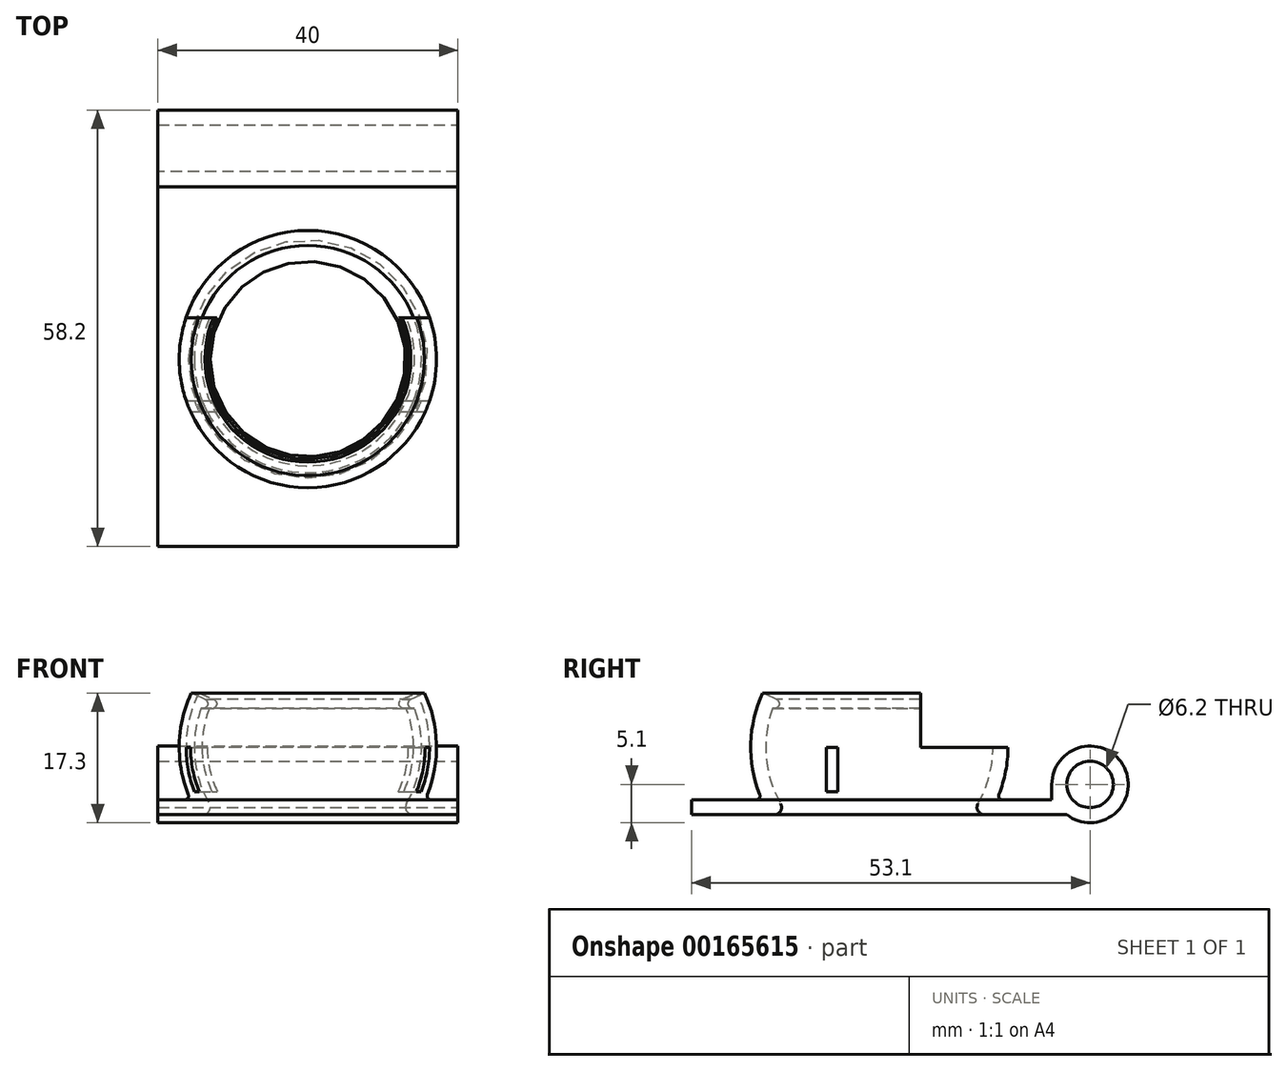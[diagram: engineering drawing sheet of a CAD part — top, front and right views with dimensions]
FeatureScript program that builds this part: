
annotation { "Feature Type Name" : "Feature", "Feature Type Description" : "" }
export const myFeature = defineFeature(function(context is Context, id is Id, definition is map)
    precondition{}
    {
        {
            var Q0;
            Q0=qCreatedBy(makeId("Front.planeOp"),FACE);
            var sketch = newSketch(context, id + "F0", { "sketchPlane" : qUnion([Q0])});
            skArc(sketch, "E0", {"start": v(-4.55, 14.3) * mm, "mid": v(-14.58, 3.55) * mm, "end": v(-10.6, -10.6) * mm});
            skLineSegment(sketch, "E1", {"start": v(-4.55, 14.3) * mm, "end": v(-4.55, 0) * mm});
            skLineSegment(sketch, "E2", {"start": v(-4.55, 0) * mm, "end": v(-3.05, 0) * mm});
            skLineSegment(sketch, "E3", {"start": v(-3.05, 0) * mm, "end": v(-3.05, -2) * mm});
            skLineSegment(sketch, "E4", {"start": v(-3.05, -2) * mm, "end": v(-6.55, -2) * mm});
            skLineSegment(sketch, "E5", {"start": v(-6.55, -2) * mm, "end": v(-6.55, 11.23) * mm});
            skArc(sketch, "E6", {"start": v(-6.55, 11.23) * mm, "mid": v(-12.9, 1.67) * mm, "end": v(-9.2, -9.2) * mm});
            skLineSegment(sketch, "E7", {"start": v(-9.2, -9.2) * mm, "end": v(-10.6, -10.6) * mm});
            skLineSegment(sketch, "E8", {"start": v(0, 0) * mm, "end": v(0, 15.93) * mm, "construction": true});
            skSolve(sketch);
        }
        {
            var Q0;
            Q0=sQuery(id+"F0.wireOp",EDGE,"E6");
            var Q1;
            Q1=sQuery(id+"F0.wireOp",EDGE,"E7");
            var Q2;
            Q2=sQuery(id+"F0.wireOp",EDGE,"E0");
            var Q3;
            Q3=sQuery(id+"F0.wireOp",EDGE,"E1");
            var Q4;
            Q4=sQuery(id+"F0.wireOp",EDGE,"E5");
            var Q5;
            Q5=sQuery(id+"F0.wireOp",EDGE,"E4");
            var Q6;
            Q6=sQuery(id+"F0.wireOp",EDGE,"E3");
            var Q7;
            Q7=sQuery(id+"F0.wireOp",EDGE,"E2");
            var Q8;
            Q8=sQuery(id+"F0.wireOp",EDGE,"E8");
            revolve(context, id + "F1", {"bodyType" : ToolBodyType.SURFACE, "surfaceEntities" : qUnion([Q0, Q1, Q2, Q3, Q4, Q5, Q6, Q7]), "axis" : qUnion([Q8]), "revolveType" : RevolveType.FULL});
        }
        {
            var Q0;
            Q0=qCreatedBy(makeId("Front.planeOp"),FACE);
            var sketch = newSketch(context, id + "F2", { "sketchPlane" : qUnion([Q0])});
            skArc(sketch, "E9", {"start": v(-15.54, 7.25) * mm, "mid": v(-17.14, 0.5) * mm, "end": v(-15.94, -6.32) * mm});
            skLineSegment(sketch, "E10", {"start": v(-14.03, -9) * mm, "end": v(-20, -9) * mm});
            skLineSegment(sketch, "E11", {"start": v(-20, -9) * mm, "end": v(-20, -7) * mm});
            skLineSegment(sketch, "E12", {"start": v(-20, -7) * mm, "end": v(-16.4, -7) * mm});
            skPoint(sketch, "E13.visualSharp", {"position": v(-12.19, -9) * mm});
            skArc(sketch, "E13.filletArc", {"start": v(-14.03, -9) * mm, "mid": v(-13.16, -8.5) * mm, "end": v(-13.16, -7.5) * mm});
            skPoint(sketch, "E14.visualSharp", {"position": v(-15.66, -7) * mm});
            skArc(sketch, "E14.filletArc", {"start": v(-16.4, -7) * mm, "mid": v(-16, -6.78) * mm, "end": v(-15.94, -6.32) * mm});
            skLineSegment(sketch, "E15", {"start": v(0, -14.05) * mm, "end": v(0, 8.9) * mm, "construction": true});
            skLineSegment(sketch, "E16", {"start": v(-13.73, 6.4) * mm, "end": v(-15.54, 7.25) * mm});
            skArc(sketch, "E17", {"start": v(-14.22, 5.22) * mm, "mid": v(-13.4, 5.57) * mm, "end": v(-13.73, 6.4) * mm});
            skArc(sketch, "E18.trimOffspring", {"start": v(-14.22, 5.22) * mm, "mid": v(-15.1, -1.26) * mm, "end": v(-13.16, -7.5) * mm});
            skSolve(sketch);
        }
        {
            var Q0;
            Q0=makeQuery(id+"F2.imprint","IMPRINT",FACE,{"disambiguationData":[TD([[makeQuery(id+"F2.imprint","IMPRINT",EDGE,{"derivedFrom":sQuery(id+"F2.wireOp",EDGE,"E9")}),1.0]])]});
            var Q1;
            Q1=sQuery(id+"F2.wireOp",EDGE,"E15");
            revolve(context, id + "F3", {"entities" : qUnion([Q0]), "axis" : qUnion([Q1]), "revolveType" : RevolveType.FULL});
        }
        {
            var Q0;
            Q0=qCreatedBy(makeId("Top.planeOp"),FACE);
            var sketch = newSketch(context, id + "F4", { "sketchPlane" : qUnion([Q0])});
            skLineSegment(sketch, "E19.bottom", {"start": v(-18.77, 18.77) * mm, "end": v(18.58, 18.77) * mm});
            skLineSegment(sketch, "E19.top", {"start": v(-18.77, 5.52) * mm, "end": v(18.58, 5.52) * mm});
            skLineSegment(sketch, "E19.left", {"start": v(-18.77, 18.77) * mm, "end": v(-18.77, 5.52) * mm});
            skLineSegment(sketch, "E19.right", {"start": v(18.58, 18.77) * mm, "end": v(18.58, 5.52) * mm});
            skSolve(sketch);
        }
        {
            var Q0;
            Q0=makeQuery(id+"F4.imprint","IMPRINT",FACE,{"disambiguationData":[TD([[makeQuery(id+"F4.imprint","IMPRINT",EDGE,{"derivedFrom":sQuery(id+"F4.wireOp",EDGE,"E19.bottom")}),-1.0]])]});
            extrude(context, id + "F5", {"entities" : qUnion([Q0]), "operationType" : NewBodyOperationType.REMOVE, "depth" : 25 * mm});
        }
        {
            var Q0;
            Q0=qCreatedBy(makeId("Right.planeOp"),FACE);
            var sketch = newSketch(context, id + "F6", { "sketchPlane" : qUnion([Q0])});
            skLineSegment(sketch, "E20.bottom", {"start": v(-5.55, 0) * mm, "end": v(-7.03, 0) * mm});
            skLineSegment(sketch, "E20.top", {"start": v(-5.55, -5.9) * mm, "end": v(-7.03, -5.9) * mm});
            skLineSegment(sketch, "E20.left", {"start": v(-5.55, 0) * mm, "end": v(-5.55, -5.9) * mm});
            skLineSegment(sketch, "E20.right", {"start": v(-7.03, 0) * mm, "end": v(-7.03, -5.9) * mm});
            skSolve(sketch);
        }
        {
            var Q0;
            Q0=qSketchRegion(id+"F6",true);
            extrude(context, id + "F7", {"entities" : qUnion([Q0]), "operationType" : NewBodyOperationType.REMOVE, "endBound" : BoundingType.SYMMETRIC, "oppositeDirection" : true, "depth" : 50 * mm});
        }
        {
            var Q0;
            Q0=makeQuery(id+"F3.opRevolve","SWEPT_FACE",FACE,{"disambiguationData":[OSD([sQuery(id+"F2.wireOp",EDGE,"E10")])]});
            var sketch = newSketch(context, id + "F8", { "sketchPlane" : qUnion([Q0])});
            skLineSegment(sketch, "E21.bottom", {"start": v(20, 25) * mm, "end": v(-20, 25) * mm});
            skLineSegment(sketch, "E21.top", {"start": v(20, -25) * mm, "end": v(-20, -25) * mm});
            skLineSegment(sketch, "E21.left", {"start": v(20, 25) * mm, "end": v(20, -25) * mm});
            skLineSegment(sketch, "E21.right", {"start": v(-20, 25) * mm, "end": v(-20, -25) * mm});
            skPoint(sketch, "E21.middle", {"position": v(0, 0) * mm});
            skCircle(sketch, "E22", {"center": v(0, 0) * mm, "radius": 19.03 * mm});
            skSolve(sketch);
        }
        {
            var Q0;
            Q0=makeQuery(id+"F8.imprint","IMPRINT",FACE,{"disambiguationData":[TD([[makeQuery(id+"F8.imprint","IMPRINT",EDGE,{"derivedFrom":sQuery(id+"F8.wireOp",EDGE,"E21.bottom")}),1.0]])]});
            var Q1;
            {var subQ0=sQuery(id+"F8.wireOp",EDGE,"E21.top");Q1=makeQuery(id+"F8.imprint","IMPRINT",FACE,{"disambiguationData":[TD([[makeQuery(id+"F8.imprint","IMPRINT",EDGE,{"derivedFrom":subQ0}),-1.0]])]});}
            extrude(context, id + "F9", {"entities" : qUnion([Q0, Q1]), "operationType" : NewBodyOperationType.ADD, "oppositeDirection" : true, "depth" : 2 * mm});
        }
        {
            var Q0;
            {var subQ0=sQuery(id+"F8.wireOp",EDGE,"E21.left");Q0=makeQuery(id+"F9.boolean.opBoolean","MERGE",FACE,{"derivedFrom":[makeQuery(id+"F9.opExtrude","SWEPT_FACE",FACE,{"disambiguationData":[OSD([subQ0]),TDD([makeQuery(id+"F8.imprint","IMPRINT",EDGE,{"disambiguationData":[TD([[makeQuery(id+"F8.imprint","INTERSECT",VERTEX,{"derivedFrom":[sQuery(id+"F8.wireOp",EDGE,"E21.bottom"),subQ0]}),-1.0]])],"derivedFrom":subQ0})])]}),makeQuery(id+"F9.opExtrude","SWEPT_FACE",FACE,{"disambiguationData":[OSD([subQ0]),TDD([makeQuery(id+"F8.imprint","IMPRINT",EDGE,{"disambiguationData":[TD([[makeQuery(id+"F8.imprint","INTERSECT",VERTEX,{"derivedFrom":[sQuery(id+"F8.wireOp",EDGE,"E21.top"),subQ0]}),1.0]])],"derivedFrom":subQ0})])]})]});}
            var sketch = newSketch(context, id + "F10", { "sketchPlane" : qUnion([Q0])});
            skLineSegment(sketch, "E23.bottom", {"start": v(25, -7) * mm, "end": v(23, -7) * mm});
            skLineSegment(sketch, "E23.left", {"start": v(25, -9) * mm, "end": v(25, -7) * mm});
            skLineSegment(sketch, "E23.right", {"start": v(23, -7) * mm, "end": v(23, -4.95) * mm});
            skArc(sketch, "E24", {"start": v(25, -9) * mm, "mid": v(32.67, -2.7) * mm, "end": v(23, -4.95) * mm});
            skCircle(sketch, "E25", {"center": v(28.1, -4.95) * mm, "radius": 3.1 * mm});
            skSolve(sketch);
        }
        {
            var Q0;
            Q0=makeQuery(id+"F10.imprint","IMPRINT",FACE,{"disambiguationData":[TD([[makeQuery(id+"F10.imprint","IMPRINT",EDGE,{"derivedFrom":sQuery(id+"F10.wireOp",EDGE,"E23.bottom")}),1.0]])]});
            extrude(context, id + "F11", {"entities" : qUnion([Q0]), "operationType" : NewBodyOperationType.ADD, "oppositeDirection" : true, "depth" : 40 * mm});
        }
    });
